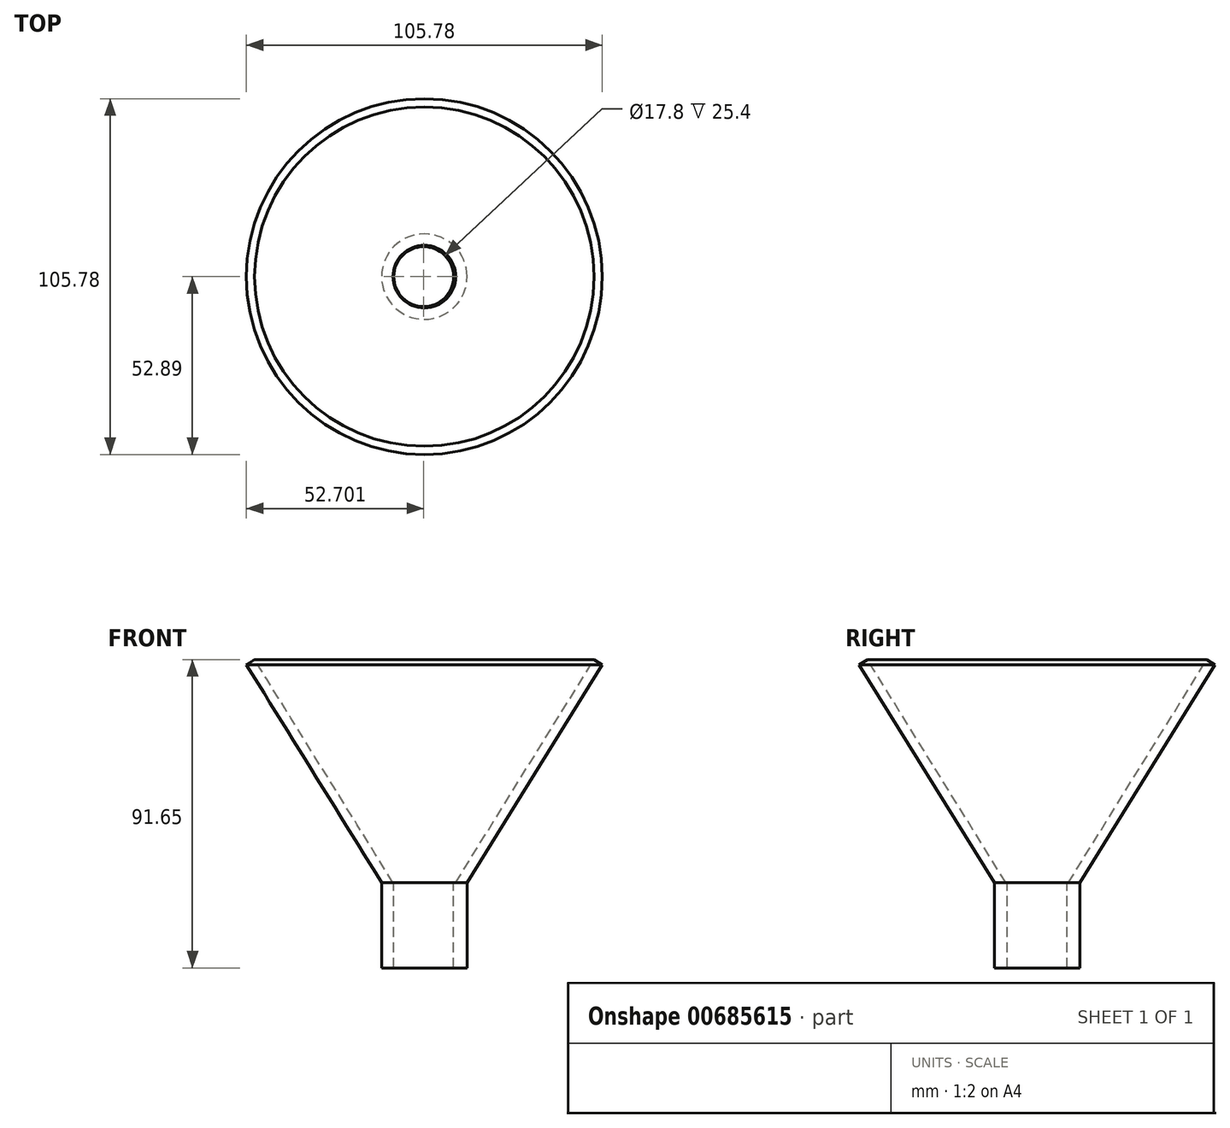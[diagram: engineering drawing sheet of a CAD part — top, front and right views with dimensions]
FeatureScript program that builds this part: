
annotation { "Feature Type Name" : "Feature", "Feature Type Description" : "" }
export const myFeature = defineFeature(function(context is Context, id is Id, definition is map)
    precondition{}
    {
        {
            var Q0;
            Q0=qCreatedBy(makeId("Front.planeOp"),FACE);
            var sketch = newSketch(context, id + "F0", { "sketchPlane" : qUnion([Q0])});
            skLineSegment(sketch, "E0", {"start": v(0, 0) * mm, "end": v(40.2, 64.74) * mm});
            skLineSegment(sketch, "E1", {"start": v(40.2, 64.74) * mm, "end": v(37.75, 66.25) * mm});
            skLineSegment(sketch, "E2", {"start": v(37.75, 66.25) * mm, "end": v(-3.38, 0) * mm});
            skLineSegment(sketch, "E3", {"start": v(0, 0) * mm, "end": v(0, -25.4) * mm});
            skLineSegment(sketch, "E4", {"start": v(0, -25.4) * mm, "end": v(-12.7, -25.4) * mm});
            skLineSegment(sketch, "E5", {"start": v(-12.7, -25.4) * mm, "end": v(-12.7, 0) * mm});
            skLineSegment(sketch, "E6", {"start": v(-12.7, 0) * mm, "end": v(-3.38, 0) * mm});
            skSolve(sketch);
        }
        {
            var Q0;
            Q0=makeQuery(id+"F0.imprint","IMPRINT",FACE,{"disambiguationData":[TD([[makeQuery(id+"F0.imprint","IMPRINT",EDGE,{"derivedFrom":sQuery(id+"F0.wireOp",EDGE,"E0")}),1.0]])]});
            var Q1;
            Q1=sQuery(id+"F0.wireOp",EDGE,"E5");
            revolve(context, id + "F1", {"entities" : qUnion([Q0]), "axis" : qUnion([Q1]), "revolveType" : RevolveType.FULL});
        }
        {
            var Q0;
            Q0=makeQuery(id+"F1.opRevolve","SWEPT_FACE",FACE,{"disambiguationData":[OSD([sQuery(id+"F0.wireOp",EDGE,"E6")])]});
            var sketch = newSketch(context, id + "F2", { "sketchPlane" : qUnion([Q0])});
            skCircle(sketch, "E7", {"center": v(-12.7, 0) * mm, "radius": 7.58 * mm});
            skSolve(sketch);
        }
        {
            var Q0;
            Q0 = qSketchRegion(id + "F2", true);
            extrude(context, id + "F3", {"entities" : qUnion([Q0]), "operationType" : NewBodyOperationType.REMOVE, "oppositeDirection" : true, "depth" : 25.4 * mm, "offsetDistance" : 25.4 * mm});
        }
        {
            var Q0;
            Q0=qCreatedBy(makeId("Top.planeOp"),FACE);
            var sketch = newSketch(context, id + "F4", { "sketchPlane" : qUnion([Q0])});
            skCircle(sketch, "E8", {"center": v(-12.89, 0) * mm, "radius": 8.9 * mm});
            skSolve(sketch);
        }
        {
            var Q0;
            Q0 = qSketchRegion(id + "F4", true);
            extrude(context, id + "F5", {"entities" : qUnion([Q0]), "operationType" : NewBodyOperationType.REMOVE, "oppositeDirection" : true, "depth" : 25.4 * mm, "offsetDistance" : 25.4 * mm});
        }
    });
